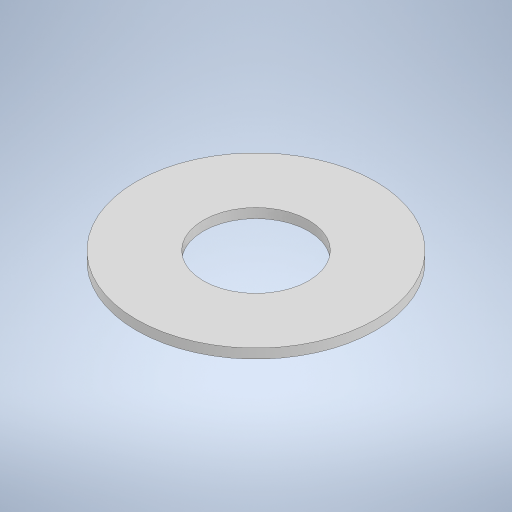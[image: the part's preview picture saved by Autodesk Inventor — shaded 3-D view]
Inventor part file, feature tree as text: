
AUTODESK INVENTOR PART (.ipt)
format: ipt  version: 2024.2 (Build 282272000, 272)  size: 220,160 bytes
history: native  units: mm
features: extrude x1, sketch x1
ambient origin geometry x8: Origin, YZ Plane, XZ Plane, XY Plane, X Axis, Y Axis, Z Axis, Center Point
bodies: Solid1 (feature_tree)
feature tree (2):
  extrude  "Extrusion1"  Depth=0.2mm
  sketch  "Sketch1"  dims[d0=2.2mm d1=5.0mm d2=0.2mm d3=0.0mm]
